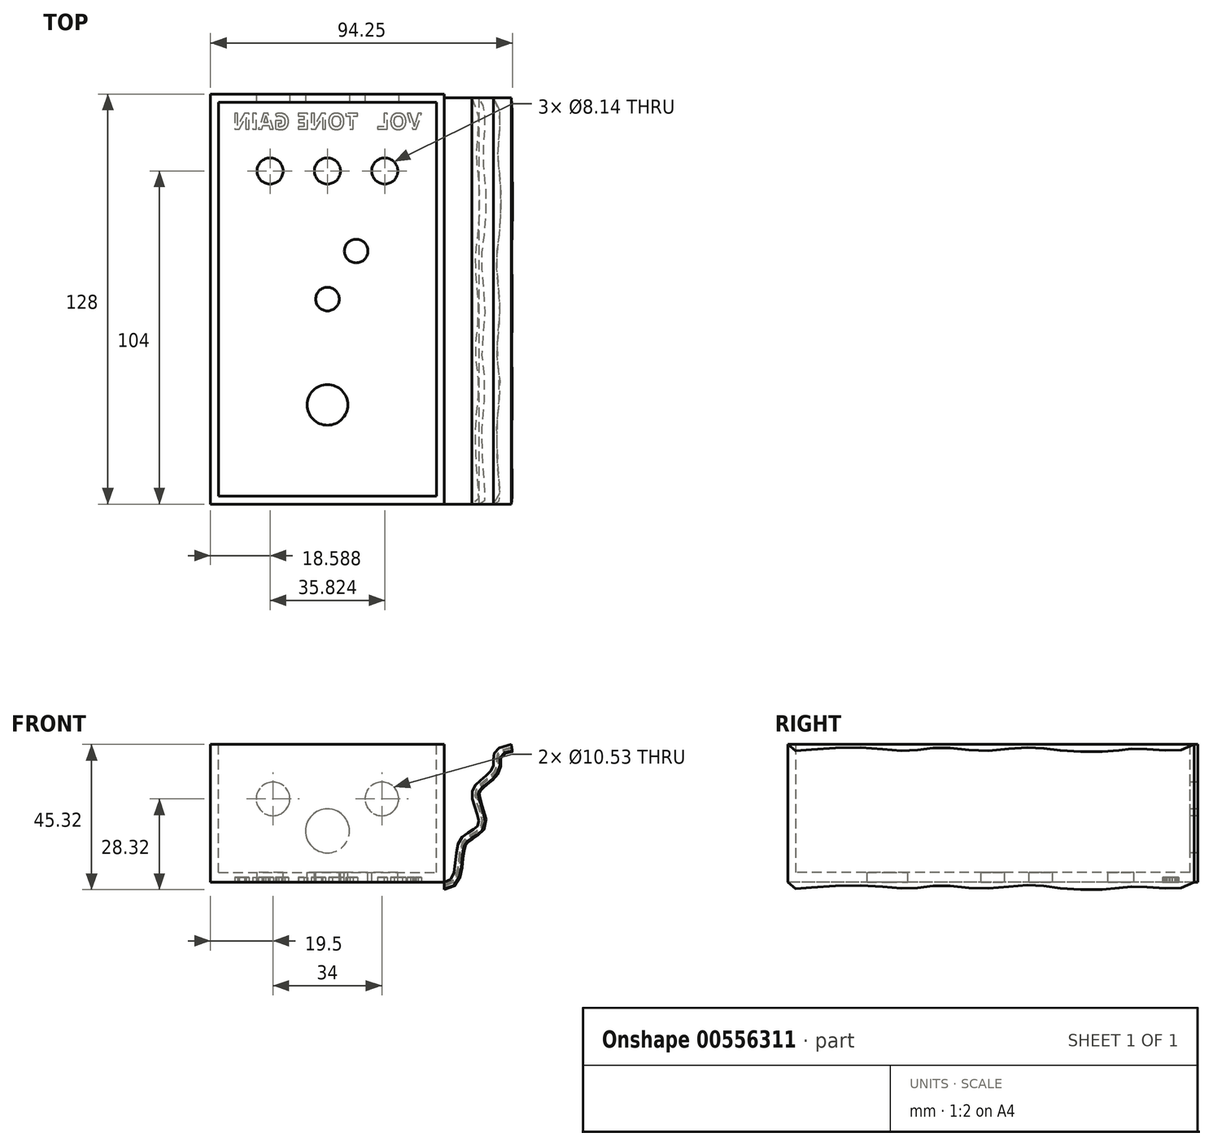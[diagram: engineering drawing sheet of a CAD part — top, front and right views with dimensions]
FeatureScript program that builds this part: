
annotation { "Feature Type Name" : "Feature", "Feature Type Description" : "" }
export const myFeature = defineFeature(function(context is Context, id is Id, definition is map)
    precondition{}
    {
        {
            var Q0;
            Q0=qCreatedBy(makeId("Top.planeOp"),FACE);
            var sketch = newSketch(context, id + "F0", { "sketchPlane" : qUnion([Q0])});
            skLineSegment(sketch, "E0.bottom", {"start": v(-36.5, 64) * mm, "end": v(36.5, 64) * mm});
            skLineSegment(sketch, "E0.top", {"start": v(-36.5, -64) * mm, "end": v(36.5, -64) * mm});
            skLineSegment(sketch, "E0.left", {"start": v(-36.5, 64) * mm, "end": v(-36.5, -64) * mm});
            skLineSegment(sketch, "E0.right", {"start": v(36.5, 64) * mm, "end": v(36.5, -64) * mm});
            skSolve(sketch);
        }
        {
            var Q0;
            Q0=makeQuery(id+"F0.imprint","IMPRINT",FACE,{"disambiguationData":[TD([[makeQuery(id+"F0.imprint","IMPRINT",EDGE,{"derivedFrom":sQuery(id+"F0.wireOp",EDGE,"E0.bottom")}),-1.0]])]});
            extrude(context, id + "F1", {"entities" : qUnion([Q0]), "depth" : 43 * mm, "offsetDistance" : 25 * mm});
        }
        {
            var Q0;
            Q0=makeQuery(id+"F1.opExtrude","CAP_FACE",FACE,{"disambiguationData":[OSD([sQuery(id+"F0.wireOp",EDGE,"E0.bottom"),sQuery(id+"F0.wireOp",EDGE,"E0.top"),sQuery(id+"F0.wireOp",EDGE,"E0.left"),sQuery(id+"F0.wireOp",EDGE,"E0.right")])],"isStart":false});
            var sketch = newSketch(context, id + "F2", { "sketchPlane" : qUnion([Q0])});
            skLineSegment(sketch, "E1.bottom", {"start": v(-34, 61.5) * mm, "end": v(34, 61.5) * mm});
            skLineSegment(sketch, "E1.top", {"start": v(-34, -61.5) * mm, "end": v(34, -61.5) * mm});
            skLineSegment(sketch, "E1.left", {"start": v(-34, 61.5) * mm, "end": v(-34, -61.5) * mm});
            skLineSegment(sketch, "E1.right", {"start": v(34, 61.5) * mm, "end": v(34, -61.5) * mm});
            skSolve(sketch);
        }
        {
            var Q0;
            Q0=makeQuery(id+"F2.imprint","IMPRINT",FACE,{"disambiguationData":[TD([[makeQuery(id+"F2.imprint","IMPRINT",EDGE,{"derivedFrom":sQuery(id+"F2.wireOp",EDGE,"E1.bottom")}),-1.0]])]});
            extrude(context, id + "F3", {"entities" : qUnion([Q0]), "operationType" : NewBodyOperationType.REMOVE, "oppositeDirection" : true, "depth" : 40 * mm, "offsetDistance" : 25 * mm});
        }
        {
            var Q0;
            Q0=makeQuery(id+"F3.boolean.opBoolean","COPY",FACE,{"derivedFrom":makeQuery(id+"F3.opExtrude","CAP_FACE",FACE,{"disambiguationData":[OSD([sQuery(id+"F2.wireOp",EDGE,"E1.bottom"),sQuery(id+"F2.wireOp",EDGE,"E1.top"),sQuery(id+"F2.wireOp",EDGE,"E1.left"),sQuery(id+"F2.wireOp",EDGE,"E1.right")])],"isStart":false})});
            var sketch = newSketch(context, id + "F4", { "sketchPlane" : qUnion([Q0])});
            skCircle(sketch, "E2", {"center": v(-17.91, 40) * mm, "radius": 4.07 * mm});
            skCircle(sketch, "E3", {"center": v(0, 40) * mm, "radius": 4.07 * mm});
            skCircle(sketch, "E4", {"center": v(17.91, 40) * mm, "radius": 4.07 * mm});
            skCircle(sketch, "E5", {"center": v(0, -33) * mm, "radius": 6.35 * mm});
            skLineSegment(sketch, "E6", {"start": v(17.91, 40) * mm, "end": v(0, 40) * mm, "construction": true});
            skLineSegment(sketch, "E7", {"start": v(8.96, 40) * mm, "end": v(8.96, 15.16) * mm, "construction": true});
            skCircle(sketch, "E8", {"center": v(8.96, 15) * mm, "radius": 3.67 * mm});
            skCircle(sketch, "E9", {"center": v(0, 0) * mm, "radius": 3.67 * mm});
            skSolve(sketch);
        }
        {
            var Q0;
            Q0=qSketchRegion(id+"F4",true);
            extrude(context, id + "F5", {"entities" : qUnion([Q0]), "operationType" : NewBodyOperationType.REMOVE, "oppositeDirection" : true, "depth" : 25 * mm, "offsetDistance" : 25 * mm});
        }
        {
            var Q0;
            Q0=makeQuery(id+"F3.boolean.opBoolean","COPY",FACE,{"derivedFrom":makeQuery(id+"F3.opExtrude","SWEPT_FACE",FACE,{"disambiguationData":[OSD([sQuery(id+"F2.wireOp",EDGE,"E1.bottom")])]})});
            var sketch = newSketch(context, id + "F6", { "sketchPlane" : qUnion([Q0])});
            skCircle(sketch, "E10", {"center": v(0, 16) * mm, "radius": 6.85 * mm});
            skCircle(sketch, "E11", {"center": v(17, 26) * mm, "radius": 5.26 * mm});
            skCircle(sketch, "E12", {"center": v(-17, 26) * mm, "radius": 5.26 * mm});
            skSolve(sketch);
        }
        {
            var Q0;
            Q0=qSketchRegion(id+"F6",true);
            extrude(context, id + "F7", {"entities" : qUnion([Q0]), "operationType" : NewBodyOperationType.REMOVE, "oppositeDirection" : true, "depth" : 25 * mm, "offsetDistance" : 25 * mm});
        }
        {
            var Q0;
            Q0=qCreatedBy(makeId("Front.planeOp"),FACE);
            cPlane(context, id + "F8", {"entities" : qUnion([Q0]), "cplaneType" : CPlaneType.OFFSET, "offset" : 38 * mm, "width" : 150 * mm, "height" : 150 * mm});
        }
        {
            var Q0;
            Q0=makeQuery(id+"F1.opExtrude","CAP_FACE",FACE,{"disambiguationData":[OSD([sQuery(id+"F0.wireOp",EDGE,"E0.bottom"),sQuery(id+"F0.wireOp",EDGE,"E0.top"),sQuery(id+"F0.wireOp",EDGE,"E0.left"),sQuery(id+"F0.wireOp",EDGE,"E0.right")])],"isStart":true});
            var sketch = newSketch(context, id + "F9", { "sketchPlane" : qUnion([Q0])});
            skText(sketch, "E13", { "text": "VOL", "fontName": "OpenSans-Bold.ttf"});
            skText(sketch, "E14", { "text": "TONE", "fontName": "OpenSans-Bold.ttf"});
            skText(sketch, "E15", { "text": "GAIN", "fontName": "OpenSans-Bold.ttf"});
            const initialGuessF9  = {"E13": [0.0294, -0.053, -1, 0, 0.005], "E14": [0.00956, -0.053, -1, 0, 0.005], "E15": [-0.0118, -0.053, -1, 0, 0.005]};
            skSetInitialGuess(sketch, initialGuessF9);
            skSolve(sketch);
        }
        {
            var Q0;
            Q0=qSketchRegion(id+"F9",true);
            extrude(context, id + "F10", {"entities" : qUnion([Q0]), "operationType" : NewBodyOperationType.REMOVE, "oppositeDirection" : true, "depth" : 1.5 * mm, "offsetDistance" : 25 * mm});
        }
        {
            var Q0;
            Q0=qCreatedBy(makeId("Front.planeOp"),FACE);
            var sketch = newSketch(context, id + "F11", { "sketchPlane" : qUnion([Q0])});
            skLineSegment(sketch, "E16.0", {"start": v(36.5, 43) * mm, "end": v(36.5, 0) * mm});
            skLineSegment(sketch, "E17.0.2", {"start": v(36.5, 43) * mm, "end": v(-36.5, 43) * mm});
            skLineSegment(sketch, "E17.0.3", {"start": v(-36.5, 43) * mm, "end": v(-36.5, 0) * mm});
            skFitSpline(sketch, "E18", {"points": [v(36.5, 0) * mm, v(41.12, 12.67) * mm, v(47.17, 18.18) * mm, v(45.23, 28.53) * mm, v(51.68, 35.79) * mm, v(57.4, 43) * mm], "startDerivative": vector(59.16, 0) * mm, "endDerivative": vector(120.65, 18.11) * mm});
            skLineSegment(sketch, "E19", {"start": v(36.5, 43) * mm, "end": v(50.21, 43) * mm, "construction": true});
            skSolve(sketch);
        }
        {
            var Q0;
            Q0=makeQuery(id+"F1.opExtrude","SWEPT_FACE",FACE,{"disambiguationData":[OSD([sQuery(id+"F0.wireOp",EDGE,"E0.right")])]});
            var sketch = newSketch(context, id + "F12", { "sketchPlane" : qUnion([Q0])});
            skLineSegment(sketch, "E20", {"start": v(64, 1) * mm, "end": v(-64, 1) * mm});
            skFitSpline(sketch, "E21", {"points": [v(64, 1) * mm, v(56.47, -2) * mm, v(44.57, -1.35) * mm, v(38, -2) * mm, v(22.12, -2) * mm, v(11.49, -0.92) * mm, v(-3.18, -2) * mm, v(-16.62, -1.02) * mm, v(-26.39, -2) * mm, v(-41.4, -1) * mm, v(-60.97, -2) * mm, v(-64, 0) * mm], "startDerivative": vector(-99.79, -93.36) * mm, "endDerivative": vector(-43.26, 121.63) * mm});
            skSolve(sketch);
        }
        {
            var Q0;
            {var subQ0=sQuery(id+"F12.wireOp",EDGE,"E21");var subQ1=makeQuery(id+"F1.opExtrude","CAP_EDGE",EDGE,{"disambiguationData":[OSD([sQuery(id+"F0.wireOp",EDGE,"E0.right")])],"isStart":true});var subQ2=makeQuery(id+"F12.imprint","INTERSECT",VERTEX,{"disambiguationData":[OD(0.0)],"derivedFrom":[subQ1,subQ0]});Q0=makeQuery(id+"F12.imprint","IMPRINT",FACE,{"disambiguationData":[TD([[makeQuery(id+"F12.imprint","IMPRINT",EDGE,{"disambiguationData":[TD([[subQ2,-1.0]])],"derivedFrom":subQ0}),-1.0]])]});}
            var Q1;
            {var subQ0=sQuery(id+"F12.wireOp",EDGE,"E21");var subQ1=makeQuery(id+"F1.opExtrude","CAP_EDGE",EDGE,{"disambiguationData":[OSD([sQuery(id+"F0.wireOp",EDGE,"E0.right")])],"isStart":true});var subQ2=makeQuery(id+"F12.imprint","INTERSECT",VERTEX,{"disambiguationData":[OD(2.0)],"derivedFrom":[subQ1,subQ0]});Q1=makeQuery(id+"F12.imprint","IMPRINT",FACE,{"disambiguationData":[TD([[makeQuery(id+"F12.imprint","IMPRINT",EDGE,{"disambiguationData":[TD([[subQ2,-1.0]])],"derivedFrom":subQ0}),-1.0]])]});}
            var Q2;
            {var subQ0=sQuery(id+"F12.wireOp",EDGE,"E21");var subQ1=makeQuery(id+"F1.opExtrude","CAP_EDGE",EDGE,{"disambiguationData":[OSD([sQuery(id+"F0.wireOp",EDGE,"E0.right")])],"isStart":true});var subQ2=makeQuery(id+"F12.imprint","INTERSECT",VERTEX,{"disambiguationData":[OD(4.0)],"derivedFrom":[subQ1,subQ0]});Q2=makeQuery(id+"F12.imprint","IMPRINT",FACE,{"disambiguationData":[TD([[makeQuery(id+"F12.imprint","IMPRINT",EDGE,{"disambiguationData":[TD([[subQ2,-1.0]])],"derivedFrom":subQ0}),-1.0]])]});}
            var Q3;
            {var subQ0=sQuery(id+"F12.wireOp",EDGE,"E21");var subQ1=sQuery(id+"F0.wireOp",EDGE,"E0.right");var subQ2=makeQuery(id+"F1.opExtrude","CAP_EDGE",EDGE,{"disambiguationData":[OSD([subQ1])],"isStart":true});var subQ4=makeQuery(id+"F12.imprint","INTERSECT",VERTEX,{"disambiguationData":[OD(6.0)],"derivedFrom":[subQ2,subQ0]});Q3=makeQuery(id+"F12.imprint","IMPRINT",FACE,{"disambiguationData":[TD([[makeQuery(id+"F12.imprint","IMPRINT",EDGE,{"disambiguationData":[TD([[subQ4,-1.0]])],"derivedFrom":subQ0}),-1.0]])]});}
            var Q4;
            Q4=sQuery(id+"F11.wireOp",EDGE,"E18");
            sweep(context, id + "F13", {"operationType" : NewBodyOperationType.ADD, "profiles" : qUnion([Q0, Q1, Q2, Q3]), "path" : qUnion([Q4])});
        }
    });
